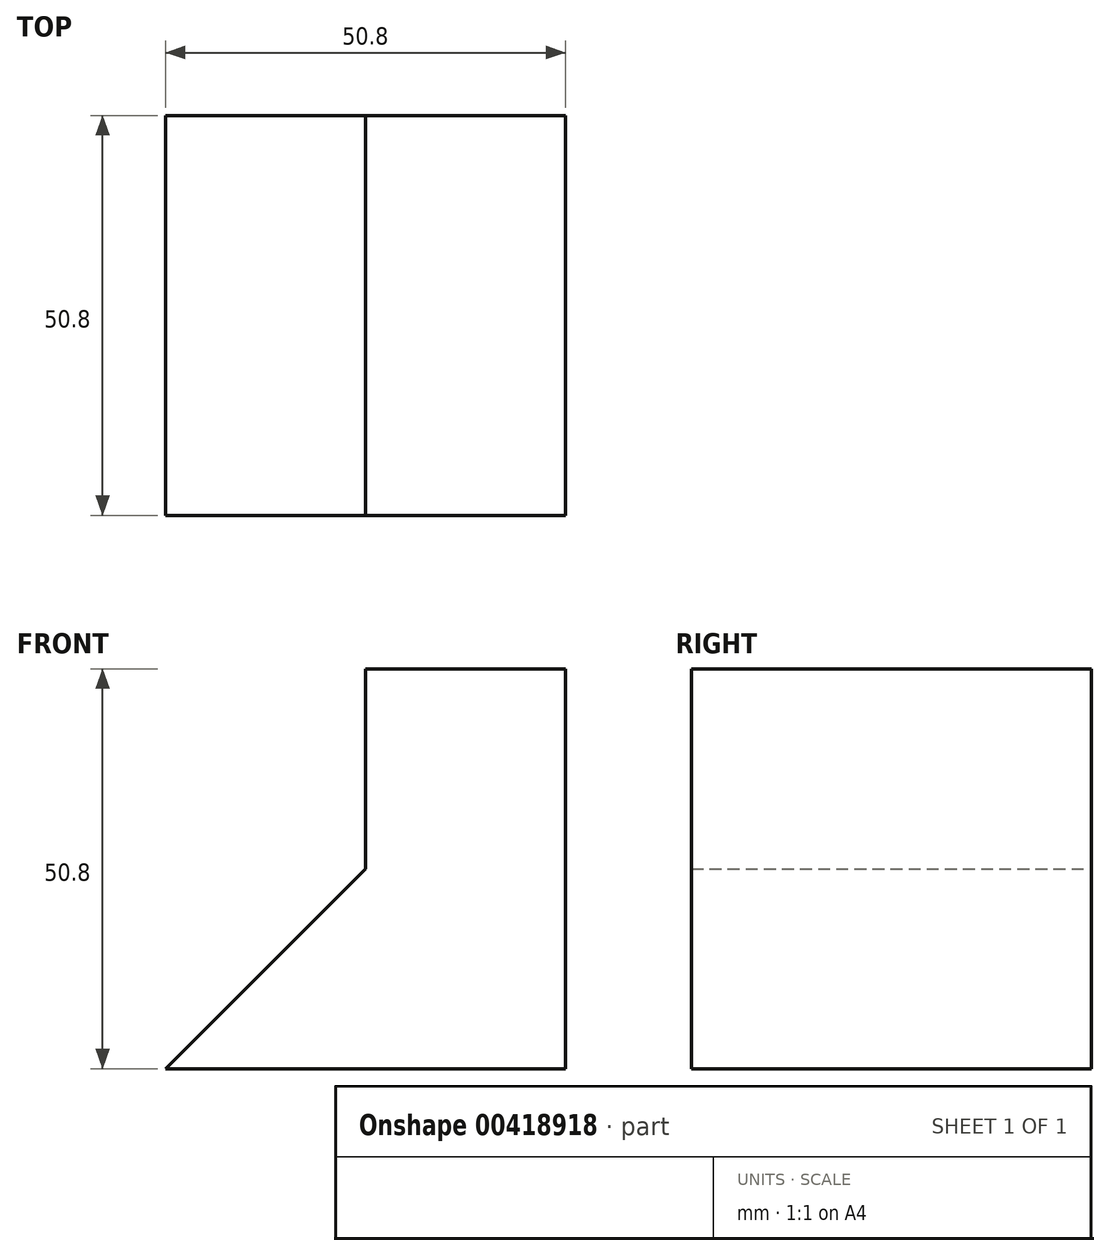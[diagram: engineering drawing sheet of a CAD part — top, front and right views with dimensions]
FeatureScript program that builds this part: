
annotation { "Feature Type Name" : "Feature", "Feature Type Description" : "" }
export const myFeature = defineFeature(function(context is Context, id is Id, definition is map)
    precondition{}
    {
        {
            var Q0;
            Q0=qCreatedBy(makeId("Front.planeOp"),FACE);
            var sketch = newSketch(context, id + "F0", { "sketchPlane" : qUnion([Q0])});
            skLineSegment(sketch, "E0", {"start": v(0, 0) * mm, "end": v(50.8, 0) * mm});
            skLineSegment(sketch, "E1", {"start": v(50.8, 0) * mm, "end": v(50.8, 50.8) * mm});
            skLineSegment(sketch, "E2", {"start": v(50.8, 50.8) * mm, "end": v(25.4, 50.8) * mm});
            skLineSegment(sketch, "E3", {"start": v(25.4, 50.8) * mm, "end": v(25.4, 25.4) * mm});
            skLineSegment(sketch, "E4", {"start": v(25.4, 25.4) * mm, "end": v(0, 0) * mm});
            skSolve(sketch);
        }
        {
            var Q0;
            Q0=makeQuery(id+"F0.imprint","IMPRINT",FACE,{"disambiguationData":[TD([[makeQuery(id+"F0.imprint","IMPRINT",EDGE,{"derivedFrom":sQuery(id+"F0.wireOp",EDGE,"E0")}),1.0]])]});
            extrude(context, id + "F1", {"entities" : qUnion([Q0]), "depth" : 50.8 * mm});
        }
    });
